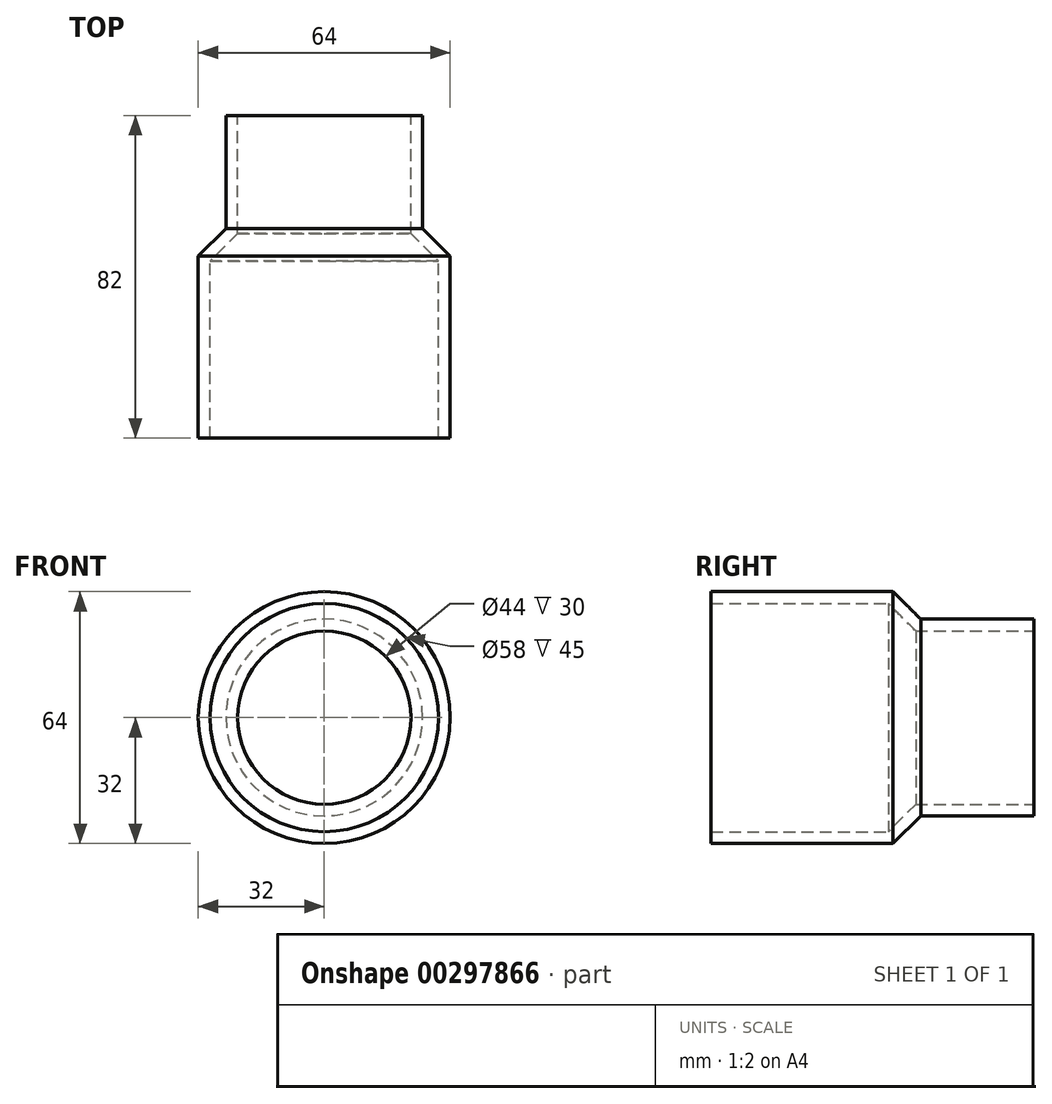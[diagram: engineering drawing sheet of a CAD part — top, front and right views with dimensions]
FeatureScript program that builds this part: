
annotation { "Feature Type Name" : "Feature", "Feature Type Description" : "" }
export const myFeature = defineFeature(function(context is Context, id is Id, definition is map)
    precondition{}
    {
        {
            var Q0;
            Q0=qCreatedBy(makeId("Top.planeOp"),FACE);
            var sketch = newSketch(context, id + "F0", { "sketchPlane" : qUnion([Q0])});
            skLineSegment(sketch, "E0", {"start": v(22, 0) * mm, "end": v(22, -30) * mm});
            skLineSegment(sketch, "E1", {"start": v(22, -30) * mm, "end": v(29, -37) * mm});
            skLineSegment(sketch, "E2", {"start": v(29, -37) * mm, "end": v(29, -82) * mm});
            skLineSegment(sketch, "E3.0", {"start": v(32, -35.76) * mm, "end": v(32, -82) * mm});
            skLineSegment(sketch, "E3.1", {"start": v(25, -28.76) * mm, "end": v(32, -35.76) * mm});
            skLineSegment(sketch, "E3.2", {"start": v(25, 0) * mm, "end": v(25, -28.76) * mm});
            skLineSegment(sketch, "E4", {"start": v(22, 0) * mm, "end": v(25, 0) * mm});
            skLineSegment(sketch, "E5", {"start": v(29, -82) * mm, "end": v(32, -82) * mm});
            skLineSegment(sketch, "E6", {"start": v(0, 0) * mm, "end": v(0, -74.97) * mm});
            skSolve(sketch);
        }
        {
            var Q0;
            Q0=makeQuery(id+"F0.imprint","IMPRINT",FACE,{"disambiguationData":[TD([[makeQuery(id+"F0.imprint","IMPRINT",EDGE,{"derivedFrom":sQuery(id+"F0.wireOp",EDGE,"E0")}),1.0]])]});
            var Q1;
            Q1=sQuery(id+"F0.wireOp",EDGE,"E6");
            revolve(context, id + "F1", {"entities" : qUnion([Q0]), "axis" : qUnion([Q1]), "revolveType" : RevolveType.FULL});
        }
    });
